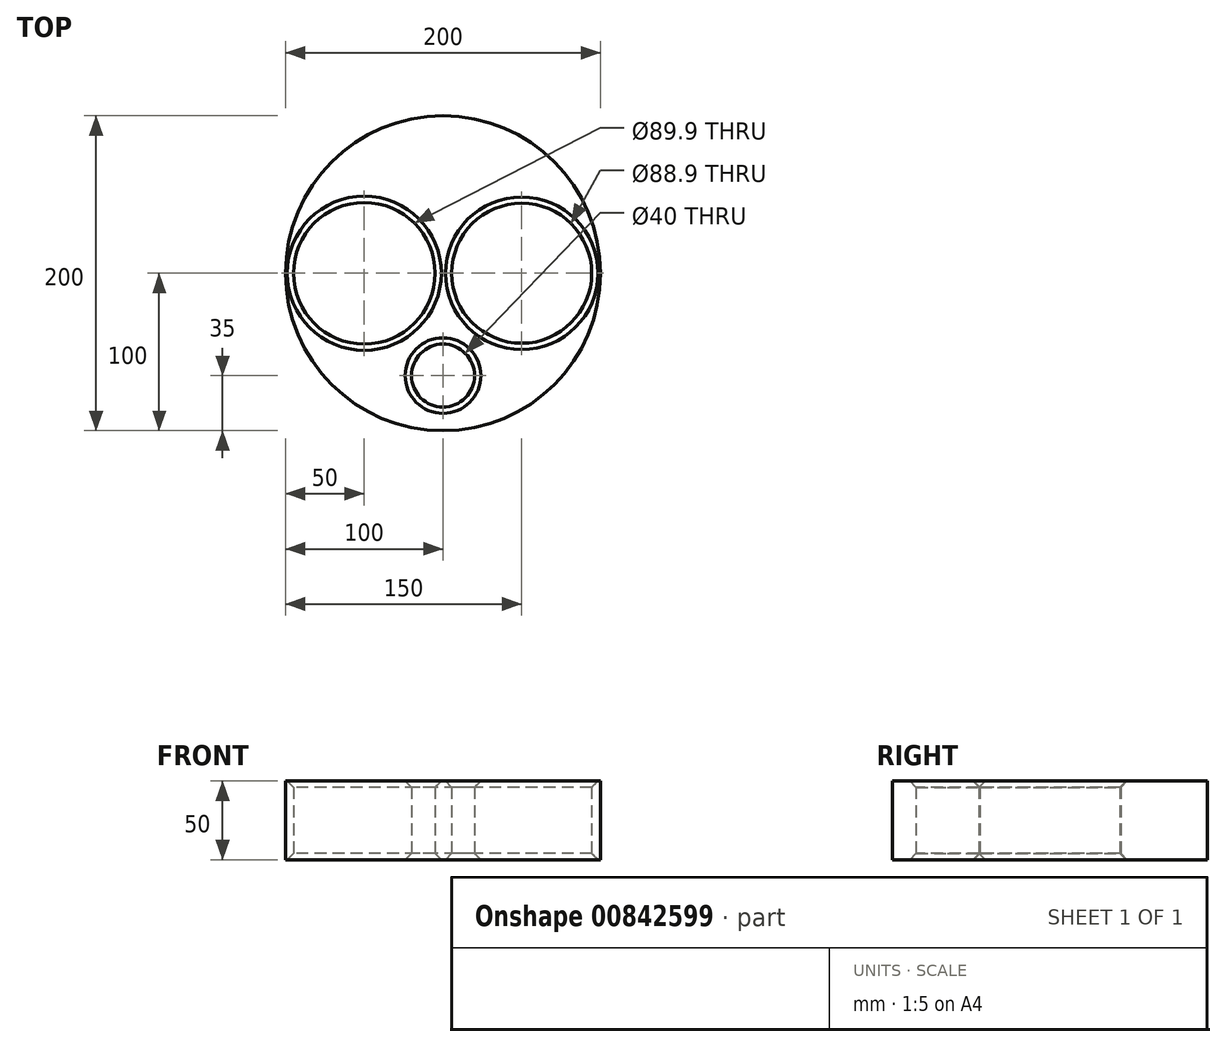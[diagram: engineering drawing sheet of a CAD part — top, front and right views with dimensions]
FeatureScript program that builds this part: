
annotation { "Feature Type Name" : "Feature", "Feature Type Description" : "" }
export const myFeature = defineFeature(function(context is Context, id is Id, definition is map)
    precondition{}
    {
        {
            var Q0;
            Q0=qCreatedBy(makeId("Top.planeOp"),FACE);
            var sketch = newSketch(context, id + "F0", { "sketchPlane" : qUnion([Q0])});
            skCircle(sketch, "E0", {"center": v(0, 0) * mm, "radius": 100 * mm});
            skCircle(sketch, "E1", {"center": v(-50, 0) * mm, "radius": 44.95 * mm});
            skCircle(sketch, "E2", {"center": v(50, 0) * mm, "radius": 44.45 * mm});
            skCircle(sketch, "E3", {"center": v(0, -65) * mm, "radius": 20 * mm});
            skSolve(sketch);
        }
        {
            var Q0;
            Q0 = qSketchRegion(id + "F0", true);
            extrude(context, id + "F1", {"entities" : qUnion([Q0]), "depth" : 50 * mm, "offsetDistance" : 25 * mm});
        }
        {
            var Q0;
            Q0=makeQuery(id+"F1.opExtrude","CAP_EDGE",EDGE,{"disambiguationData":[OSD([sQuery(id+"F0.wireOp",EDGE,"E2")])],"isStart":false});
            var Q1;
            Q1=makeQuery(id+"F1.opExtrude","CAP_EDGE",EDGE,{"disambiguationData":[OSD([sQuery(id+"F0.wireOp",EDGE,"E1")])],"isStart":false});
            var Q2;
            Q2=makeQuery(id+"F1.opExtrude","CAP_EDGE",EDGE,{"disambiguationData":[OSD([sQuery(id+"F0.wireOp",EDGE,"E3")])],"isStart":false});
            var Q3;
            Q3=makeQuery(id+"F1.opExtrude","CAP_EDGE",EDGE,{"disambiguationData":[OSD([sQuery(id+"F0.wireOp",EDGE,"E2")])],"isStart":true});
            var Q4;
            Q4=makeQuery(id+"F1.opExtrude","CAP_EDGE",EDGE,{"disambiguationData":[OSD([sQuery(id+"F0.wireOp",EDGE,"E1")])],"isStart":true});
            var Q5;
            Q5=makeQuery(id+"F1.opExtrude","CAP_EDGE",EDGE,{"disambiguationData":[OSD([sQuery(id+"F0.wireOp",EDGE,"E3")])],"isStart":true});
            chamfer(context, id + "F2", {"entities" : qUnion([Q0, Q1, Q2, Q3, Q4, Q5]), "width" : 4 * mm, "tangentPropagation" : true});
        }
    });
